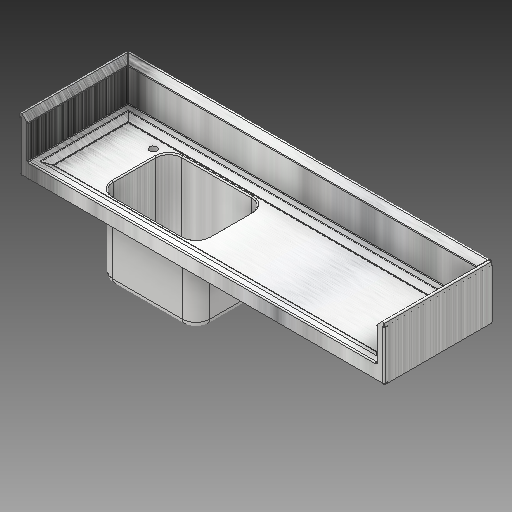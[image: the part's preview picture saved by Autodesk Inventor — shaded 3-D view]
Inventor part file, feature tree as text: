
AUTODESK INVENTOR PART (.ipt)
format: ipt  version: 2017 (Build 210142000, 142)  size: 1,063,936 bytes
history: native  units: mm
features: sheet_metal_op x40, sketch x27, other x22, extrude x9, reference x4, plane x1, hole x1, projected_geometry x1
ambient origin geometry x8: Origin, YZ Plane, XZ Plane, XY Plane, X Axis, Y Axis, Z Axis, Center Point
bodies: Solid1 (feature_tree)
feature tree (105):
  sheet_metal_op  "Face1"
  sheet_metal_op  "Flange3"
  sheet_metal_op  "Flange4"
  sheet_metal_op  "Flange5"
  extrude  "Extrusion1"  Depth=260.0mm
  sheet_metal_op  "Flange10"
  sheet_metal_op  "Flange11"
  sheet_metal_op  "Flange12"
  extrude  "Extrusion6"  Depth=1.5mm
  sheet_metal_op  "Flange13"
  sheet_metal_op  "Flange14"
  sheet_metal_op  "Flange15"
  sheet_metal_op  "Flange16"
  sheet_metal_op  "Flange17"
  plane  "Work Plane2"
  other  "Decal2"
  extrude  "Extrusion7"  Depth=1.5mm
  sheet_metal_op  "Flange18"
  sheet_metal_op  "Flange19"
  extrude  "Extrusion8"  Depth=1.5mm
  extrude  "Extrusion15"  Depth=1.5mm
  extrude  "Extrusion16"  Depth=1.5mm
  extrude  "Extrusion17"  Depth=1.5mm
  extrude  "Extrusion18"  Depth=1.5mm
  extrude  "Extrusion19"  Depth=1.5mm
  hole  "Hole1"  [1 undecoded]
  sketch  "Sketch1"  dims[d0=900.0mm d1=260.0mm]
  other  "Plate1"
  sketch  "Sketch3"  dims[d2=1.5mm d12=15.0mm d13=1.5mm]
  sketch  "Sketch7"  dims[d39=1.5mm d41=1.5mm]
  other  "Plate4"
  sheet_metal_op  "Bend3"
  sheet_metal_op  "Corner3"
  sketch  "Sketch8"  dims[d43=1.5mm d44=0.75mm]
  other  "Plate5"
  sheet_metal_op  "Bend4"
  sheet_metal_op  "Corner4"
  sketch  "Sketch9"  dims[d45=3.0mm d46=1.5mm]
  other  "Plate6"
  sheet_metal_op  "Bend5"
  sheet_metal_op  "Corner5"
  sketch  "Sketch10"  dims[d47=86.0mm d48=90.0deg d49=1.5mm d50=6.0mm]
  sketch  "Sketch21"  dims[d51=1.5mm d52=1.5mm]
  other  "Plate11"
  sheet_metal_op  "Bend10"
  sheet_metal_op  "Corner10"
  sketch  "Sketch22"  dims[d53=1.5mm d54=0.75mm]
  other  "Plate12"
  sheet_metal_op  "Bend11"
  sheet_metal_op  "Corner11"
  sketch  "Sketch23"  dims[d55=3.0mm d56=1.5mm]
  other  "Plate13"
  sheet_metal_op  "Bend12"
  sheet_metal_op  "Corner12"
  sketch  "Sketch24"  dims[d57=28.0mm d58=45.0deg d59=1.5mm d60=6.0mm]
  sketch  "Sketch25"  dims[d61=1.5mm]
  other  "Plate14"
  sheet_metal_op  "Bend13"
  sheet_metal_op  "Corner13"
  sketch  "Sketch26"  dims[d62=1.5mm]
  other  "Plate15"
  sheet_metal_op  "Bend14"
  sheet_metal_op  "Corner14"
  sketch  "Sketch27"  dims[d63=1.5mm]
  other  "Plate16"
  sheet_metal_op  "Bend15"
  sheet_metal_op  "Corner15"
  sketch  "Sketch28"  dims[d64=0.75mm]
  other  "Plate17"
  sheet_metal_op  "Bend16"
  sheet_metal_op  "Corner16"
  sketch  "Sketch29"  dims[d65=3.0mm]
  other  "Plate18"
  sheet_metal_op  "Bend17"
  sheet_metal_op  "Corner17"
  sketch  "Sketch30"  dims[d66=1.5mm]
  other  "Image2"
  sketch  "Sketch31"  dims[d67=16.0mm d68=135.0deg d69=1.5mm]
  sketch  "Sketch32"  dims[d70=6.0mm]
  other  "Plate19"
  sheet_metal_op  "Bend18"
  sheet_metal_op  "Corner18"
  sketch  "Sketch33"  dims[d71=1.5mm]
  other  "Plate20"
  sheet_metal_op  "Bend19"
  sheet_metal_op  "Corner19"
  sketch  "Sketch34"  dims[d72=1.5mm]
  projected_geometry  "Projected Loop7"
  sketch  "Sketch35"  dims[d74=130.0mm]
  sketch  "Sketch42"  dims[d75=19.05mm]
  sketch  "Sketch43"  dims[d76=1.5mm]
  sketch  "Sketch44"  dims[d77=0.0mm]
  sketch  "Sketch45"  dims[d145=0.0mm]
  sketch  "Sketch46"  dims[d147=270.0mm]
  sketch  "Sketch47"  dims[d148=20.0mm d149=20.0mm d150=0.0mm d151=1.5mm d152=0.75mm d153=3.0mm d154=1.5mm d155=40.0mm d156=90.0deg d157=1.5mm d158=6.0mm d159=1.5mm d160=1.5mm d161=1.5mm d162=0.75mm d163=3.0mm d164=1.5mm d165=10.0mm d166=90.0deg d167=1.5mm d168=6.0mm d169=1.5mm d170=1.5mm d171=1.5mm d172=0.75mm d173=3.0mm d174=1.5mm d175=19.799mm d176=90.0deg d177=1.5mm d178=6.0mm d179=1.5mm d180=1.5mm d181=1.5mm d182=0.0mm d183=1.5mm d184=0.75mm d185=3.0mm d186=1.5mm d187=19.799mm d188=0.0mm d189=1.5mm d190=6.0mm d191=1.5mm d192=1.5mm d193=1.5mm d194=0.75mm d195=3.0mm d196=1.5mm d197=41.5mm d198=0.0mm d199=1.5mm d200=6.0mm d201=1.5mm d202=1.5mm d203=1.5mm d204=0.75mm d205=3.0mm d206=1.5mm d207=10.0mm d208=90.0deg d209=1.5mm d210=6.0mm d211=1.5mm d212=1.5mm d213=1.5mm d214=0.75mm d215=3.0mm d216=1.5mm d217=4.5mm d218=0.0mm d219=1.5mm d220=6.0mm d221=1.5mm d222=1.5mm d223=1.5mm d224=0.75mm d225=3.0mm d226=1.5mm d227=4.5mm d228=0.0mm d229=1.5mm d230=6.0mm d231=1.5mm d232=1.5mm d233=400.0mm d239=1.5mm d240=0.0mm d241=1.5mm d242=0.75mm d243=3.0mm d244=1.5mm d245=0.0mm d246=10.0mm d247=10.0mm d248=90.0deg d249=1.5mm d250=6.0mm d251=1.5mm d252=1.5mm d253=1.5mm d254=0.75mm d255=3.0mm d256=1.5mm d257=8.0mm d258=0.0mm d259=10.0mm d260=90.0deg d261=1.5mm d262=6.0mm d263=1.5mm d264=1.5mm d266=15.0mm d267=1.5mm d269=1.5mm d270=1.5mm d272=1.5mm d273=0.0mm d274=0.0mm d287=10.0mm d288=0.0mm d289=10.0mm d290=0.0mm d291=10.0mm d292=0.0mm d293=10.0mm d294=0.0mm d295=40.0mm d296=268.0mm d297=40.0mm d298=268.0mm d299=1.5mm d300=0.0mm d301=6.647mm d302=16.0mm d303=4.0mm d304=2.0mm d305=90.0deg d306=22.2mm d307=20.594885mm]
  reference  "Reference1"
  reference  "Reference2"
  reference  "Reference3"
  reference  "Reference4"
  other  "iFeature1:1"
  other  "iFeature5:1"
  other  "iFeature1:3"
  other  "Bancada de Lavagem Mãos - 1150 x 370 x 900h.iam"
  other  "Lateral -A1:1"
  other  "Lateral -A:1"
note: 1 required parameter value undecoded (feature->parameter linkage not recoverable at this tier; creation-order binding heuristic only, values carry confidence <= 0.55)
